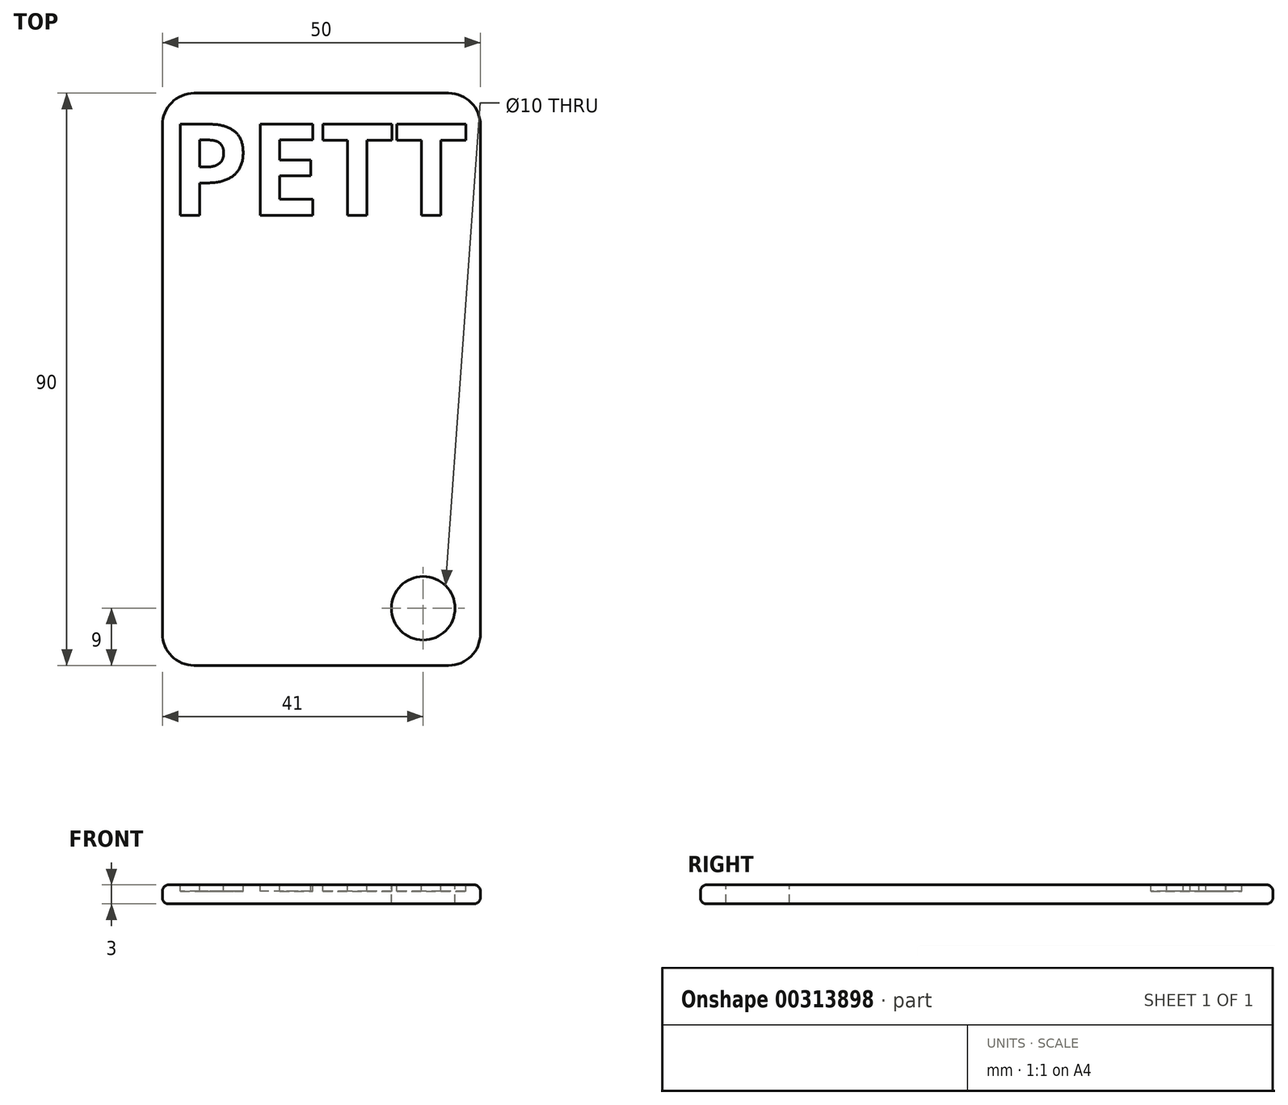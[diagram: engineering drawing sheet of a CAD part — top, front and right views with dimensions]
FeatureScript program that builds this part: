
annotation { "Feature Type Name" : "Feature", "Feature Type Description" : "" }
export const myFeature = defineFeature(function(context is Context, id is Id, definition is map)
    precondition{}
    {
        {
            var Q0;
            Q0=qCreatedBy(makeId("Top.planeOp"),FACE);
            var sketch = newSketch(context, id + "F0", { "sketchPlane" : qUnion([Q0])});
            skLineSegment(sketch, "E0.bottom", {"start": v(-45, 25) * mm, "end": v(45, 25) * mm});
            skLineSegment(sketch, "E0.top", {"start": v(-45, -25) * mm, "end": v(45, -25) * mm});
            skLineSegment(sketch, "E0.left", {"start": v(-45, 25) * mm, "end": v(-45, -25) * mm});
            skLineSegment(sketch, "E0.right", {"start": v(45, 25) * mm, "end": v(45, -25) * mm});
            skLineSegment(sketch, "E1", {"start": v(-45, 25) * mm, "end": v(45, -25) * mm, "construction": true});
            skSolve(sketch);
        }
        {
            var Q0;
            Q0=makeQuery(id+"F0.imprint","IMPRINT",FACE,{"disambiguationData":[TD([[makeQuery(id+"F0.imprint","IMPRINT",EDGE,{"derivedFrom":sQuery(id+"F0.wireOp",EDGE,"E0.bottom")}),-1.0]])]});
            extrude(context, id + "F1", {"entities" : qUnion([Q0]), "depth" : 3 * mm});
        }
        {
            var Q0;
            Q0=makeQuery(id+"F1.opExtrude","CAP_FACE",FACE,{"disambiguationData":[OSD([sQuery(id+"F0.wireOp",EDGE,"E0.bottom"),sQuery(id+"F0.wireOp",EDGE,"E0.top"),sQuery(id+"F0.wireOp",EDGE,"E0.left"),sQuery(id+"F0.wireOp",EDGE,"E0.right")])],"isStart":false});
            var Q1;
            Q1=makeQuery(id+"F1.opExtrude","CAP_FACE",FACE,{"disambiguationData":[OSD([sQuery(id+"F0.wireOp",EDGE,"E0.bottom"),sQuery(id+"F0.wireOp",EDGE,"E0.top"),sQuery(id+"F0.wireOp",EDGE,"E0.left"),sQuery(id+"F0.wireOp",EDGE,"E0.right")])],"isStart":true});
            fillet(context, id + "F2", {"entities" : qUnion([Q0, Q1]), "radius" : 1 * mm, "tangentPropagation" : true, "allowEdgeOverflow" : false});
        }
        {
            var Q0;
            Q0=makeQuery(id+"F1.opExtrude","SWEPT_EDGE",EDGE,{"disambiguationData":[OSD([sQuery(id+"F0.wireOp",EDGE,"E0.top"),sQuery(id+"F0.wireOp",EDGE,"E0.right")])]});
            var Q1;
            Q1=makeQuery(id+"F1.opExtrude","SWEPT_EDGE",EDGE,{"disambiguationData":[OSD([sQuery(id+"F0.wireOp",EDGE,"E0.bottom"),sQuery(id+"F0.wireOp",EDGE,"E0.right")])]});
            var Q2;
            Q2=makeQuery(id+"F1.opExtrude","SWEPT_EDGE",EDGE,{"disambiguationData":[OSD([sQuery(id+"F0.wireOp",EDGE,"E0.bottom"),sQuery(id+"F0.wireOp",EDGE,"E0.left")])]});
            var Q3;
            Q3=makeQuery(id+"F1.opExtrude","SWEPT_EDGE",EDGE,{"disambiguationData":[OSD([sQuery(id+"F0.wireOp",EDGE,"E0.top"),sQuery(id+"F0.wireOp",EDGE,"E0.left")])]});
            fillet(context, id + "F3", {"entities" : qUnion([Q0, Q1, Q2, Q3]), "radius" : 5 * mm, "tangentPropagation" : true, "allowEdgeOverflow" : false});
        }
        {
            var Q0;
            Q0=qCreatedBy(makeId("Right.planeOp"),FACE);
            var sketch = newSketch(context, id + "F4", { "sketchPlane" : qUnion([Q0])});
            skLineSegment(sketch, "E2", {"start": v(0, 0) * mm, "end": v(0, 32.9) * mm});
            skSolve(sketch);
        }
        {
            var Q0;
            Q0=makeQuery(id+"F1.opExtrude","SWEPT_BODY",BODY,{"disambiguationData":[OSD([sQuery(id+"F0.wireOp",EDGE,"E0.bottom"),sQuery(id+"F0.wireOp",EDGE,"E0.top"),sQuery(id+"F0.wireOp",EDGE,"E0.left"),sQuery(id+"F0.wireOp",EDGE,"E0.right")])]});
            var Q1;
            Q1=sQuery(id+"F4.wireOp",EDGE,"E2");
            transform(context, id + "F5", {"entities" : qUnion([Q0]), "transformType" : TransformType.ROTATION, "transformAxis" : qUnion([Q1]), "angle" : 90 * degree, "makeCopy" : false});
        }
        {
            var Q0;
            Q0=makeQuery(id+"F1.opExtrude","CAP_FACE",FACE,{"disambiguationData":[OSD([sQuery(id+"F0.wireOp",EDGE,"E0.bottom"),sQuery(id+"F0.wireOp",EDGE,"E0.top"),sQuery(id+"F0.wireOp",EDGE,"E0.left"),sQuery(id+"F0.wireOp",EDGE,"E0.right")])],"isStart":false});
            var sketch = newSketch(context, id + "F6", { "sketchPlane" : qUnion([Q0])});
            skText(sketch, "E3", { "text": "PETT", "fontName": "OpenSans-Bold.ttf"});
            const initialGuessF6  = {"E3": [-0.024, 0.0258, 1, 0, 0.01445]};
            skSetInitialGuess(sketch, initialGuessF6);
            skSolve(sketch);
        }
        {
            var Q0;
            Q0=qSketchRegion(id+"F6",true);
            extrude(context, id + "F7", {"entities" : qUnion([Q0]), "operationType" : NewBodyOperationType.REMOVE, "oppositeDirection" : true, "depth" : 1 * mm});
        }
        {
            var Q0;
            {var subQ0=sQuery(id+"F0.wireOp",EDGE,"E0.left");var subQ2=sQuery(id+"F0.wireOp",EDGE,"E0.bottom");var subQ4=sQuery(id+"F0.wireOp",EDGE,"E0.right");var subQ6=sQuery(id+"F0.wireOp",EDGE,"E0.top");Q0=makeQuery(id+"F7.boolean.opBoolean","SPLIT",FACE,{"disambiguationData":[TD([makeQuery(id+"F7.opExtrude","SWEPT_FACE",FACE,{"disambiguationData":[OSD([sQuery(id+"F6.wireOp",EDGE,"E3.sketch_text.stroke-0")])]})])],"derivedFrom":makeQuery(id+"F1.opExtrude","CAP_FACE",FACE,{"disambiguationData":[OSD([subQ2,subQ6,subQ0,subQ4])],"isStart":false})});}
            var sketch = newSketch(context, id + "F8", { "sketchPlane" : qUnion([Q0])});
            skCircle(sketch, "E4", {"center": v(16, -36) * mm, "radius": 5 * mm});
            skSolve(sketch);
        }
        {
            var Q0;
            Q0=qSketchRegion(id+"F8",true);
            extrude(context, id + "F9", {"entities" : qUnion([Q0]), "operationType" : NewBodyOperationType.REMOVE, "oppositeDirection" : true, "depth" : 3 * mm});
        }
    });
